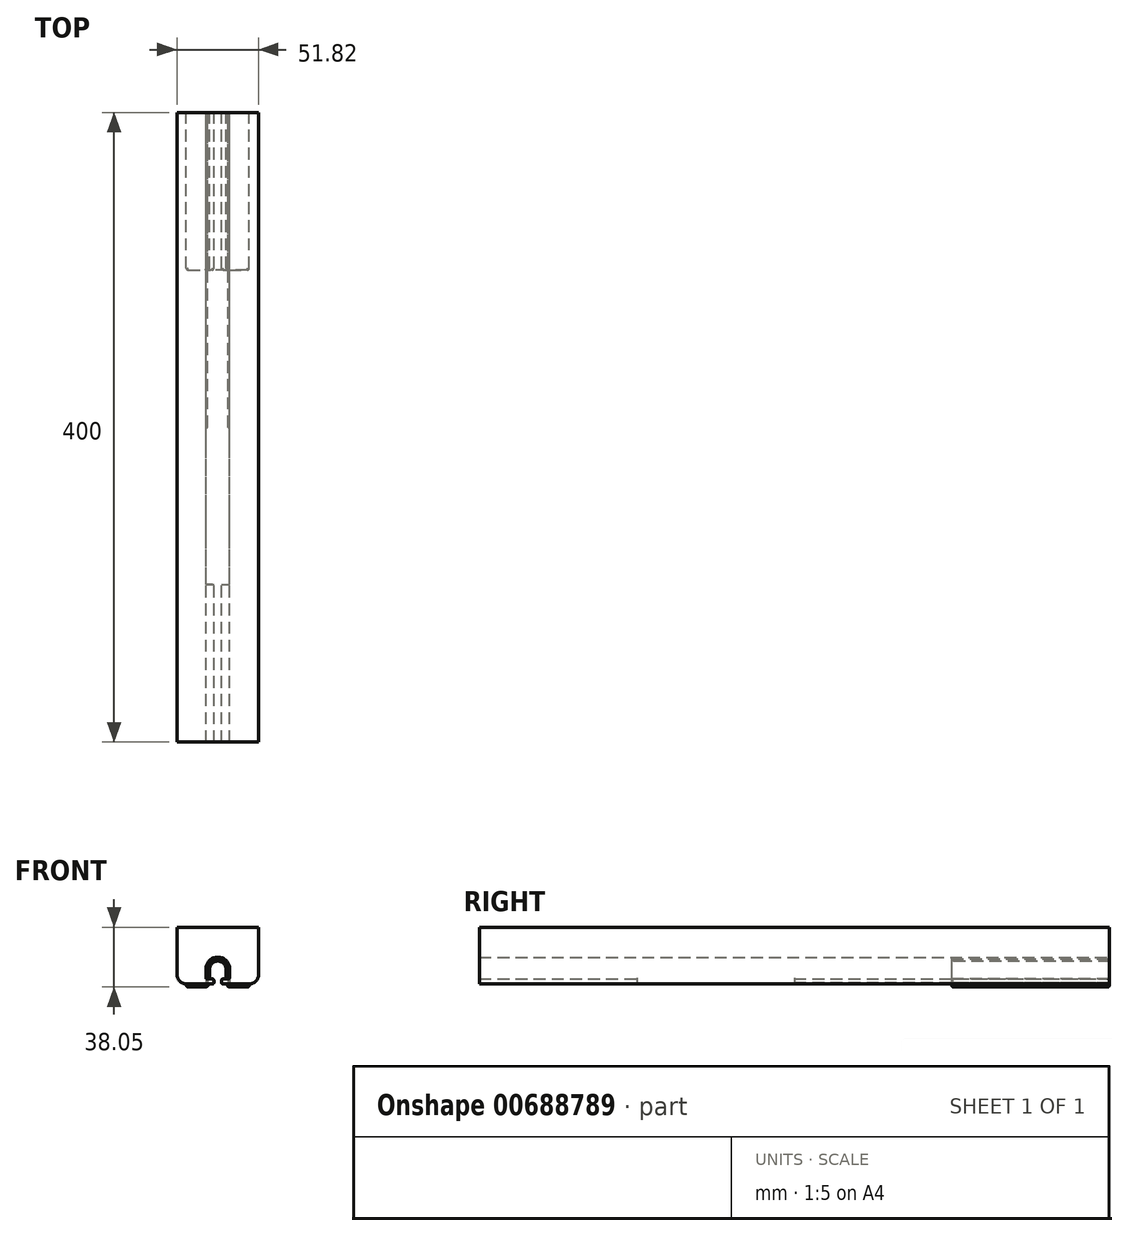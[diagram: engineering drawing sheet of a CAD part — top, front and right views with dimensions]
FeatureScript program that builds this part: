
annotation { "Feature Type Name" : "Feature", "Feature Type Description" : "" }
export const myFeature = defineFeature(function(context is Context, id is Id, definition is map)
    precondition{}
    {
        {
            var Q0;
            Q0=qCreatedBy(makeId("Front.planeOp"),FACE);
            var sketch = newSketch(context, id + "F0", { "sketchPlane" : qUnion([Q0])});
            skLineSegment(sketch, "E0", {"start": v(-20, 0) * mm, "end": v(-7.5, 0) * mm});
            skLineSegment(sketch, "E1", {"start": v(-7.5, 3.88) * mm, "end": v(-7.5, 9.5) * mm});
            skLineSegment(sketch, "E2", {"start": v(7.5, 9.5) * mm, "end": v(7.5, 3.88) * mm});
            skLineSegment(sketch, "E3", {"start": v(7.5, 0) * mm, "end": v(20, 0) * mm});
            skArc(sketch, "E4", {"start": v(-7.5, 9.5) * mm, "mid": v(0, 17) * mm, "end": v(7.5, 9.5) * mm});
            skLineSegment(sketch, "E5", {"start": v(-25.9, 5.9) * mm, "end": v(-25.9, 36.05) * mm});
            skLineSegment(sketch, "E6", {"start": v(-25.9, 36.05) * mm, "end": v(25.9, 36.05) * mm});
            skLineSegment(sketch, "E7", {"start": v(25.9, 36.05) * mm, "end": v(25.9, 5.9) * mm});
            skArc(sketch, "E8", {"start": v(-25.9, 5.9) * mm, "mid": v(-24.18, 1.73) * mm, "end": v(-20, 0) * mm});
            skArc(sketch, "E9", {"start": v(20, 0) * mm, "mid": v(24.18, 1.73) * mm, "end": v(25.9, 5.9) * mm});
            skLineSegment(sketch, "E10", {"start": v(-6.75, 3.13) * mm, "end": v(-6.5, 3.13) * mm});
            skLineSegment(sketch, "E11", {"start": v(-6.5, 3.13) * mm, "end": v(-6.5, 1) * mm});
            skLineSegment(sketch, "E12", {"start": v(-6.5, 1) * mm, "end": v(-7.5, 0) * mm});
            skLineSegment(sketch, "E13", {"start": v(6.75, 3.13) * mm, "end": v(6.5, 3.13) * mm});
            skLineSegment(sketch, "E14", {"start": v(6.5, 3.13) * mm, "end": v(6.5, 1) * mm});
            skLineSegment(sketch, "E15", {"start": v(6.5, 1) * mm, "end": v(7.5, 0) * mm});
            skLineSegment(sketch, "E16", {"start": v(-6.5, 0) * mm, "end": v(6.5, 0) * mm, "construction": true});
            skPoint(sketch, "E17", {"position": v(0, 0) * mm});
            skPoint(sketch, "E18.visualSharp", {"position": v(7.5, 3.13) * mm});
            skArc(sketch, "E18.filletArc", {"start": v(6.75, 3.13) * mm, "mid": v(7.28, 3.34) * mm, "end": v(7.5, 3.88) * mm});
            skPoint(sketch, "E19.visualSharp", {"position": v(-7.5, 3.13) * mm});
            skArc(sketch, "E19.filletArc", {"start": v(-7.5, 3.88) * mm, "mid": v(-7.28, 3.34) * mm, "end": v(-6.75, 3.13) * mm});
            skSolve(sketch);
        }
        {
            var Q0;
            Q0=qSketchRegion(id+"F0",true);
            extrude(context, id + "F1", {"entities" : qUnion([Q0]), "depth" : 300 * mm, "offsetDistance" : 25 * mm});
        }
        {
            var Q0;
            Q0=makeQuery(id+"F1.opExtrude","CAP_FACE",FACE,{"disambiguationData":[OSD([sQuery(id+"F0.wireOp",EDGE,"E0"),sQuery(id+"F0.wireOp",EDGE,"E1"),sQuery(id+"F0.wireOp",EDGE,"E2"),sQuery(id+"F0.wireOp",EDGE,"E3"),sQuery(id+"F0.wireOp",EDGE,"E4"),sQuery(id+"F0.wireOp",EDGE,"E5"),sQuery(id+"F0.wireOp",EDGE,"E6"),sQuery(id+"F0.wireOp",EDGE,"E7"),sQuery(id+"F0.wireOp",EDGE,"E8"),sQuery(id+"F0.wireOp",EDGE,"E9"),sQuery(id+"F0.wireOp",EDGE,"E10"),sQuery(id+"F0.wireOp",EDGE,"E11"),sQuery(id+"F0.wireOp",EDGE,"E12"),sQuery(id+"F0.wireOp",EDGE,"E13"),sQuery(id+"F0.wireOp",EDGE,"E14"),sQuery(id+"F0.wireOp",EDGE,"E15")])],"isStart":false});
            var sketch = newSketch(context, id + "F2", { "sketchPlane" : qUnion([Q0])});
            skLineSegment(sketch, "E20.0", {"start": v(-25.9, 36.05) * mm, "end": v(25.9, 36.05) * mm});
            skLineSegment(sketch, "E20.1", {"start": v(25.9, 36.05) * mm, "end": v(25.9, 5.9) * mm});
            skArc(sketch, "E20.2", {"start": v(20, 0) * mm, "mid": v(24.18, 1.73) * mm, "end": v(25.9, 5.9) * mm});
            skLineSegment(sketch, "E20.3", {"start": v(3.25, 0) * mm, "end": v(20, 0) * mm});
            skLineSegment(sketch, "E20.4", {"start": v(7.5, 9.5) * mm, "end": v(7.5, 9.5) * mm});
            skArc(sketch, "E20.5", {"start": v(-7.5, 9.5) * mm, "mid": v(0, 17) * mm, "end": v(7.5, 9.5) * mm});
            skLineSegment(sketch, "E20.6", {"start": v(-7.5, 3.88) * mm, "end": v(-7.5, 9.5) * mm});
            skLineSegment(sketch, "E20.7", {"start": v(-25.9, 5.9) * mm, "end": v(-25.9, 36.05) * mm});
            skArc(sketch, "E20.8", {"start": v(-25.9, 5.9) * mm, "mid": v(-24.18, 1.73) * mm, "end": v(-20, 0) * mm});
            skLineSegment(sketch, "E20.9", {"start": v(-20, 0) * mm, "end": v(-3.25, 0) * mm});
            skPoint(sketch, "E21.orphan", {"position": v(-7.5, 0) * mm});
            skPoint(sketch, "E22.orphan", {"position": v(7.5, 0) * mm});
            skLineSegment(sketch, "E23", {"start": v(-2.5, 2.38) * mm, "end": v(-2.5, 0.75) * mm});
            skLineSegment(sketch, "E24", {"start": v(2.5, 2.38) * mm, "end": v(2.5, 0.75) * mm});
            skPoint(sketch, "E25.visualSharp", {"position": v(2.5, 9) * mm});
            skArc(sketch, "E25.filletArc", {"start": v(3.25, 3.13) * mm, "mid": v(2.72, 2.9) * mm, "end": v(2.5, 2.38) * mm});
            skPoint(sketch, "E26.visualSharp", {"position": v(2.5, 0) * mm});
            skArc(sketch, "E26.filletArc", {"start": v(2.5, 0.75) * mm, "mid": v(2.72, 0.22) * mm, "end": v(3.25, 0) * mm});
            skPoint(sketch, "E27.visualSharp", {"position": v(-2.5, 4) * mm});
            skArc(sketch, "E27.filletArc", {"start": v(-2.5, 2.38) * mm, "mid": v(-2.72, 2.9) * mm, "end": v(-3.25, 3.13) * mm});
            skPoint(sketch, "E28.visualSharp", {"position": v(-2.5, 0) * mm});
            skArc(sketch, "E28.filletArc", {"start": v(-3.25, 0) * mm, "mid": v(-2.72, 0.22) * mm, "end": v(-2.5, 0.75) * mm});
            skLineSegment(sketch, "E29.0", {"start": v(7.5, 9.5) * mm, "end": v(7.5, 3.88) * mm});
            skArc(sketch, "E29.1", {"start": v(6.75, 3.13) * mm, "mid": v(7.28, 3.34) * mm, "end": v(7.5, 3.88) * mm});
            skArc(sketch, "E30.0", {"start": v(-7.5, 3.88) * mm, "mid": v(-7.28, 3.34) * mm, "end": v(-6.75, 3.13) * mm});
            skLineSegment(sketch, "E31", {"start": v(3.25, 3.12) * mm, "end": v(6.75, 3.12) * mm});
            skLineSegment(sketch, "E32", {"start": v(-3.25, 3.12) * mm, "end": v(-6.75, 3.12) * mm});
            skSolve(sketch);
        }
        {
            var Q0;
            Q0 = qSketchRegion(id + "F2", true);
            extrude(context, id + "F3", {"entities" : qUnion([Q0]), "operationType" : NewBodyOperationType.ADD, "depth" : 100 * mm, "offsetDistance" : 25 * mm});
        }
        {
            var Q0;
            Q0=makeQuery(id+"F3.boolean.opBoolean","MERGE",FACE,{"derivedFrom":[makeQuery(id+"F1.opExtrude","SWEPT_FACE",FACE,{"disambiguationData":[OSD([sQuery(id+"F0.wireOp",EDGE,"E0")])]}),makeQuery(id+"F3.opExtrude","SWEPT_FACE",FACE,{"disambiguationData":[OSD([sQuery(id+"F2.wireOp",EDGE,"E20.9")])]})]});
            var sketch = newSketch(context, id + "F4", { "sketchPlane" : qUnion([Q0])});
            skLineSegment(sketch, "E33.bottom", {"start": v(7.5, 300) * mm, "end": v(-7.5, 300) * mm});
            skLineSegment(sketch, "E33.top", {"start": v(7.5, 200) * mm, "end": v(-7.5, 200) * mm});
            skLineSegment(sketch, "E33.left", {"start": v(7.5, 300) * mm, "end": v(7.5, 200) * mm});
            skLineSegment(sketch, "E33.right", {"start": v(-7.5, 300) * mm, "end": v(-7.5, 200) * mm});
            skPoint(sketch, "E33.middle", {"position": v(0, 250) * mm});
            skSolve(sketch);
        }
        {
            var Q0;
            Q0 = qSketchRegion(id + "F4", true);
            extrude(context, id + "F5", {"entities" : qUnion([Q0]), "operationType" : NewBodyOperationType.REMOVE, "oppositeDirection" : true, "depth" : 5 * mm, "offsetDistance" : 25 * mm});
        }
        {
            var Q0;
            Q0=qCreatedBy(makeId("Front.planeOp"),FACE);
            var sketch = newSketch(context, id + "F6", { "sketchPlane" : qUnion([Q0])});
            skLineSegment(sketch, "E34", {"start": v(-7.25, 4.12) * mm, "end": v(-7.25, 8.75) * mm});
            skLineSegment(sketch, "E35", {"start": v(-20, 0) * mm, "end": v(-19.76, -1.38) * mm});
            skLineSegment(sketch, "E36", {"start": v(-19.02, -2) * mm, "end": v(-7.56, -2) * mm});
            skLineSegment(sketch, "E37", {"start": v(-2.5, 0.75) * mm, "end": v(-2.5, 2.37) * mm});
            skLineSegment(sketch, "E38", {"start": v(-3.25, 3.12) * mm, "end": v(-4.5, 3.12) * mm});
            skLineSegment(sketch, "E39", {"start": v(-5.25, 3.88) * mm, "end": v(-5.25, 9.25) * mm});
            skPoint(sketch, "E40.0", {"position": v(-20, 0) * mm});
            skLineSegment(sketch, "E41", {"start": v(0, -4.43) * mm, "end": v(0, 18.25) * mm, "construction": true});
            skLineSegment(sketch, "E42.MirrorCS", {"start": v(5.25, 3.88) * mm, "end": v(5.25, 9.25) * mm});
            skLineSegment(sketch, "E43.MirrorCS", {"start": v(3.25, 3.12) * mm, "end": v(4.5, 3.13) * mm});
            skLineSegment(sketch, "E44.MirrorCS", {"start": v(7.25, 4.13) * mm, "end": v(7.25, 8.75) * mm});
            skPoint(sketch, "E45.MirrorP", {"position": v(20, 0) * mm});
            skLineSegment(sketch, "E46.MirrorCS", {"start": v(2.5, 0.75) * mm, "end": v(2.5, 2.38) * mm});
            skLineSegment(sketch, "E47.MirrorCS", {"start": v(19.02, -2) * mm, "end": v(7.56, -2) * mm});
            skLineSegment(sketch, "E48.MirrorCS", {"start": v(20, 0) * mm, "end": v(19.76, -1.38) * mm});
            skArc(sketch, "E49", {"start": v(-5.25, 9.25) * mm, "mid": v(0, 14.5) * mm, "end": v(5.25, 9.25) * mm});
            skArc(sketch, "E50", {"start": v(-7.25, 8.75) * mm, "mid": v(0, 16) * mm, "end": v(7.25, 8.75) * mm});
            skPoint(sketch, "E51.visualSharp", {"position": v(-2.5, 0) * mm});
            skPoint(sketch, "E52.visualSharp", {"position": v(2.5, 0) * mm});
            skPoint(sketch, "E53.visualSharp", {"position": v(-2.5, 3.12) * mm});
            skArc(sketch, "E53.filletArc", {"start": v(-2.5, 2.37) * mm, "mid": v(-2.72, 2.9) * mm, "end": v(-3.25, 3.12) * mm});
            skPoint(sketch, "E54.visualSharp", {"position": v(2.5, 3.12) * mm});
            skArc(sketch, "E54.filletArc", {"start": v(3.25, 3.12) * mm, "mid": v(2.72, 2.9) * mm, "end": v(2.5, 2.38) * mm});
            skPoint(sketch, "E55.visualSharp", {"position": v(-19.65, -2) * mm});
            skArc(sketch, "E55.filletArc", {"start": v(-19.76, -1.38) * mm, "mid": v(-19.5, -1.82) * mm, "end": v(-19.02, -2) * mm});
            skLineSegment(sketch, "E56", {"start": v(-3.25, 0) * mm, "end": v(-4.94, 0) * mm});
            skLineSegment(sketch, "E57", {"start": v(3.25, 0) * mm, "end": v(4.94, 0) * mm});
            skLineSegment(sketch, "E58", {"start": v(-5.47, -0.22) * mm, "end": v(-7.03, -1.78) * mm});
            skLineSegment(sketch, "E59", {"start": v(5.47, -0.22) * mm, "end": v(7.03, -1.78) * mm});
            skArc(sketch, "E60.filletArc", {"start": v(-3.25, 0) * mm, "mid": v(-2.72, 0.22) * mm, "end": v(-2.5, 0.75) * mm});
            skArc(sketch, "E61.filletArc", {"start": v(2.5, 0.75) * mm, "mid": v(2.72, 0.22) * mm, "end": v(3.25, 0) * mm});
            skPoint(sketch, "E62.visualSharp", {"position": v(-5.25, 0) * mm});
            skArc(sketch, "E62.filletArc", {"start": v(-4.94, 0) * mm, "mid": v(-5.23, -0.06) * mm, "end": v(-5.47, -0.22) * mm});
            skPoint(sketch, "E63.visualSharp", {"position": v(5.25, 0) * mm});
            skArc(sketch, "E63.filletArc", {"start": v(5.47, -0.22) * mm, "mid": v(5.23, -0.06) * mm, "end": v(4.94, 0) * mm});
            skPoint(sketch, "E64.visualSharp", {"position": v(7.25, -2) * mm});
            skArc(sketch, "E64.filletArc", {"start": v(7.03, -1.78) * mm, "mid": v(7.27, -1.94) * mm, "end": v(7.56, -2) * mm});
            skPoint(sketch, "E65.visualSharp", {"position": v(-7.25, -2) * mm});
            skArc(sketch, "E65.filletArc", {"start": v(-7.56, -2) * mm, "mid": v(-7.27, -1.94) * mm, "end": v(-7.03, -1.78) * mm});
            skPoint(sketch, "E66.visualSharp", {"position": v(19.65, -2) * mm});
            skArc(sketch, "E66.filletArc", {"start": v(19.02, -2) * mm, "mid": v(19.5, -1.82) * mm, "end": v(19.76, -1.38) * mm});
            skPoint(sketch, "E67.visualSharp", {"position": v(5.25, 3.12) * mm});
            skArc(sketch, "E67.filletArc", {"start": v(4.5, 3.12) * mm, "mid": v(5.03, 3.34) * mm, "end": v(5.25, 3.88) * mm});
            skPoint(sketch, "E68.visualSharp", {"position": v(-5.25, 3.12) * mm});
            skArc(sketch, "E68.filletArc", {"start": v(-5.25, 3.88) * mm, "mid": v(-5.03, 3.34) * mm, "end": v(-4.5, 3.12) * mm});
            skLineSegment(sketch, "E69", {"start": v(-6.4, 3.62) * mm, "end": v(-6.75, 3.62) * mm});
            skLineSegment(sketch, "E70", {"start": v(6.4, 3.63) * mm, "end": v(6.75, 3.63) * mm});
            skLineSegment(sketch, "E71.0", {"start": v(6.4, 3.63) * mm, "end": v(6.4, 0.96) * mm});
            skLineSegment(sketch, "E72.0", {"start": v(6.4, 0.96) * mm, "end": v(7.36, 0) * mm});
            skLineSegment(sketch, "E73.0", {"start": v(-6.4, 3.62) * mm, "end": v(-6.4, 0.96) * mm});
            skLineSegment(sketch, "E74.0", {"start": v(-6.4, 0.96) * mm, "end": v(-7.36, 0) * mm});
            skLineSegment(sketch, "E75.0", {"start": v(-20, 0) * mm, "end": v(-7.36, 0) * mm});
            skPoint(sketch, "E76.orphan", {"position": v(-7.5, 0) * mm});
            skLineSegment(sketch, "E77.0", {"start": v(7.36, 0) * mm, "end": v(20, 0) * mm});
            skPoint(sketch, "E78.orphan", {"position": v(7.5, 0) * mm});
            skArc(sketch, "E79.filletArc", {"start": v(6.75, 3.63) * mm, "mid": v(7.1, 3.77) * mm, "end": v(7.25, 4.13) * mm});
            skPoint(sketch, "E80.visualSharp", {"position": v(-7.25, 3.62) * mm});
            skArc(sketch, "E80.filletArc", {"start": v(-7.25, 4.12) * mm, "mid": v(-7.1, 3.77) * mm, "end": v(-6.75, 3.63) * mm});
            skSolve(sketch);
        }
        {
            var Q0;
            Q0=qSketchRegion(id+"F6",true);
            extrude(context, id + "F7", {"entities" : qUnion([Q0]), "depth" : 100 * mm, "offsetDistance" : 25 * mm});
        }
        {
            var Q0;
            Q0=makeQuery(id+"F7.opExtrude","CAP_EDGE",EDGE,{"disambiguationData":[OSD([sQuery(id+"F6.wireOp",EDGE,"E47.MirrorCS")])],"isStart":false});
            var Q1;
            Q1=makeQuery(id+"F7.opExtrude","CAP_EDGE",EDGE,{"disambiguationData":[OSD([sQuery(id+"F6.wireOp",EDGE,"E49")])],"isStart":true});
            fillet(context, id + "F8", {"entities" : qUnion([Q0, Q1]), "radius" : 1 * mm, "tangentPropagation" : true, "allowEdgeOverflow" : false});
        }
    });
